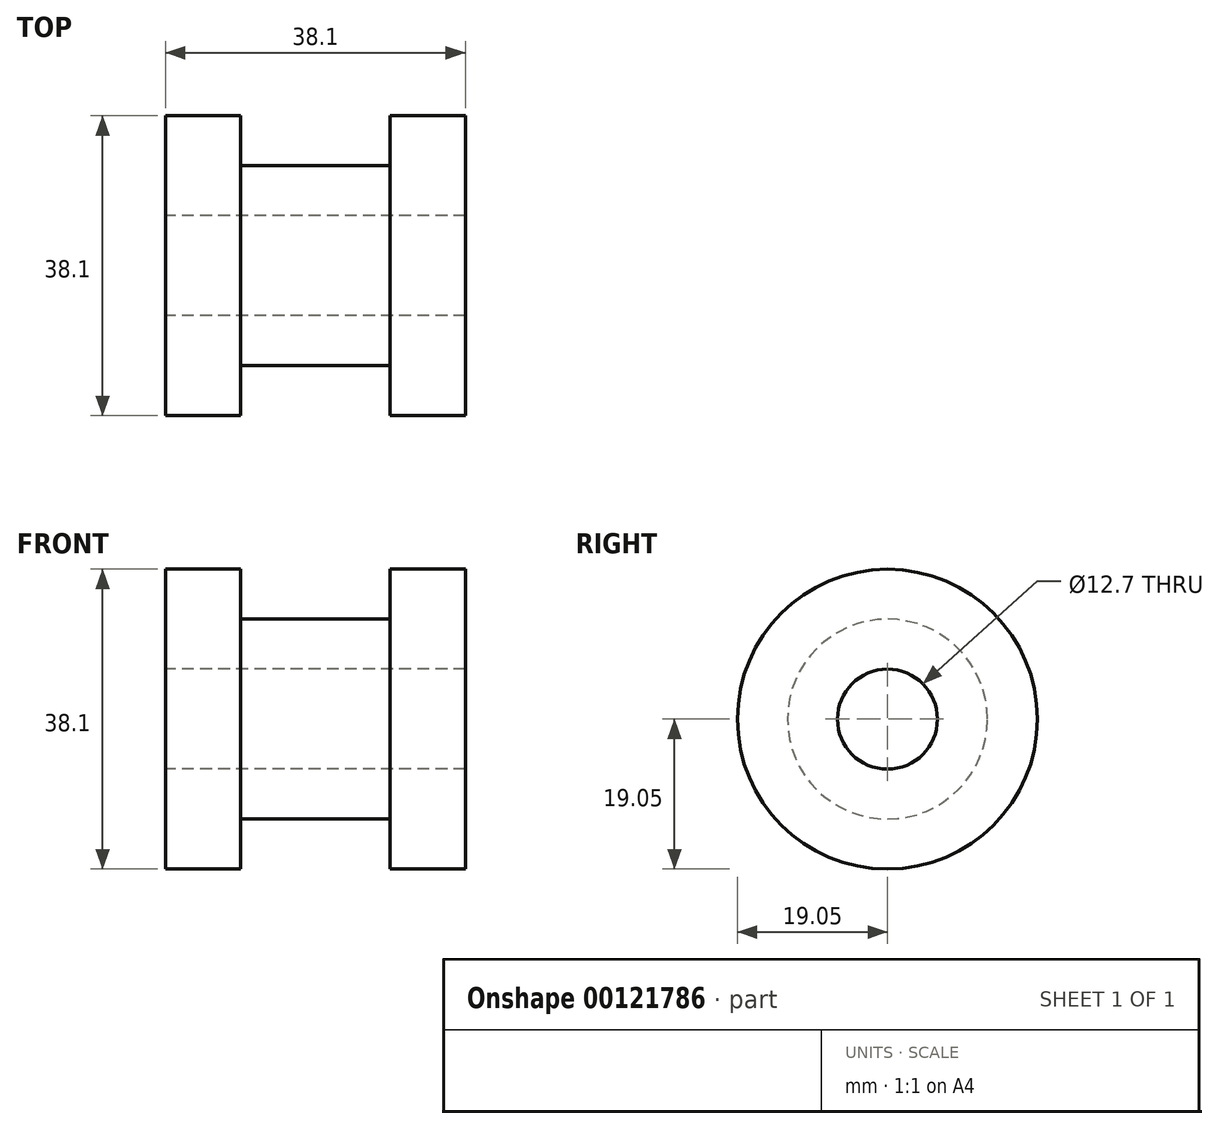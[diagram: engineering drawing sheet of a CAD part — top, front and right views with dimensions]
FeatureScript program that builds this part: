
annotation { "Feature Type Name" : "Feature", "Feature Type Description" : "" }
export const myFeature = defineFeature(function(context is Context, id is Id, definition is map)
    precondition{}
    {
        {
            var Q0;
            Q0=qCreatedBy(makeId("Front.planeOp"),FACE);
            var sketch = newSketch(context, id + "F0", { "sketchPlane" : qUnion([Q0])});
            skLineSegment(sketch, "E0", {"start": v(-19.05, 6.35) * mm, "end": v(-19.05, 19.05) * mm});
            skLineSegment(sketch, "E1", {"start": v(-19.05, 19.05) * mm, "end": v(-9.5, 19.05) * mm});
            skLineSegment(sketch, "E2", {"start": v(-9.5, 19.05) * mm, "end": v(-9.5, 12.7) * mm});
            skLineSegment(sketch, "E3", {"start": v(-9.5, 12.7) * mm, "end": v(9.5, 12.7) * mm});
            skLineSegment(sketch, "E4", {"start": v(9.5, 12.7) * mm, "end": v(9.5, 19.05) * mm});
            skLineSegment(sketch, "E5", {"start": v(9.5, 19.05) * mm, "end": v(19.05, 19.05) * mm});
            skLineSegment(sketch, "E6", {"start": v(19.05, 19.05) * mm, "end": v(19.05, 6.35) * mm});
            skLineSegment(sketch, "E7", {"start": v(19.05, 6.35) * mm, "end": v(-19.05, 6.35) * mm});
            skLineSegment(sketch, "E8", {"start": v(0, 12.7) * mm, "end": v(0, 6.35) * mm, "construction": true});
            skLineSegment(sketch, "E9", {"start": v(-1.06, 0) * mm, "end": v(79.15, 0) * mm});
            skSolve(sketch);
        }
        {
            var Q0;
            Q0 = qSketchRegion(id + "F0", true);
            var Q1;
            Q1=sQuery(id+"F0.wireOp",EDGE,"E9");
            revolve(context, id + "F1", {"entities" : qUnion([Q0]), "axis" : qUnion([Q1]), "revolveType" : RevolveType.FULL});
        }
    });
